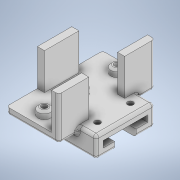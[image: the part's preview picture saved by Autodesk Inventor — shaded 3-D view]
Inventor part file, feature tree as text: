
AUTODESK INVENTOR PART (.ipt)
format: ipt  version: 2020 (Build 240168000, 168)  size: 339,968 bytes
history: native  units: in
note: dims shown in document units (in); Inventor stores cm internally (conversion verified against a paired STEP export)
features: extrude x10, sketch x10, chamfer x1, fillet x1
ambient origin geometry x8: Origin, YZ Plane, XZ Plane, XY Plane, X Axis, Y Axis, Z Axis, Center Point
bodies: Solid1 (feature_tree)
feature tree (22):
  extrude  "Extrusion1"  Depth=2.6378in
  extrude  "Extrusion2"  Depth=0.1969in
  extrude  "Extrusion6"  Depth=0.1969in
  extrude  "Extrusion8"  Depth=1.0in TaperAngle=0.0deg
  chamfer  "Chamfer1"  Distance=1.0in
  extrude  "Extrusion9"  Depth=0.3406in
  extrude  "Extrusion10"  Depth=0.1969in TaperAngle=0.0deg
  extrude  "Extrusion11"  Depth=0.1575in
  extrude  "Extrusion12"  Depth=0.1575in
  extrude  "Extrusion13"  Depth=0.0197in TaperAngle=0.0deg
  extrude  "Extrusion14"  Depth=0.0197in
  fillet  "Fillet4"  Radius=0.2362in
  sketch  "Sketch1"  dims[d0=1.4331in d1=2.6378in]
  sketch  "Sketch2"  dims[d2=0.1969in d3=0.0in d4=0.1969in]
  sketch  "Sketch6"  dims[d5=0.8268in d6=0.1969in]
  sketch  "Sketch8"  dims[d7=0.8268in d8=1.0in d9=0.0in]
  sketch  "Sketch9"  dims[d26=0.1969in]
  sketch  "Sketch10"  dims[d27=0.9449in d28=1.0in d29=0.0in]
  sketch  "Sketch11"  dims[d37=0.3406in d38=0.3406in]
  sketch  "Sketch12"  dims[d39=0.3406in d40=0.1969in d41=0.0in]
  sketch  "Sketch13"  dims[d42=0.0591in d43=0.0787in d44=45.0deg d45=0.1575in]
  sketch  "Sketch14"  dims[d46=0.1575in d47=0.1575in d48=0.7874in d49=0.0in d50=0.2362in d51=0.2362in d52=0.2362in d53=0.0984in d54=0.0in d55=1.6142in d56=0.1969in d57=0.5709in d58=0.1969in d59=0.4724in d60=0.1969in d61=0.4724in d62=0.1969in d63=0.5118in d64=1.4331in d65=0.0in d66=0.0in d67=0.1181in d68=0.1181in d69=1.4331in d70=0.0in d71=0.1575in d72=0.1575in d73=1.4331in d74=0.0in d75=0.0394in d76=0.0394in d77=0.5118in d78=0.0in d79=0.0787in d10=0.0197in d11=0.0344in d13=0.0197in d14=0.0344in d15=0.0197in d16=0.0344in]
